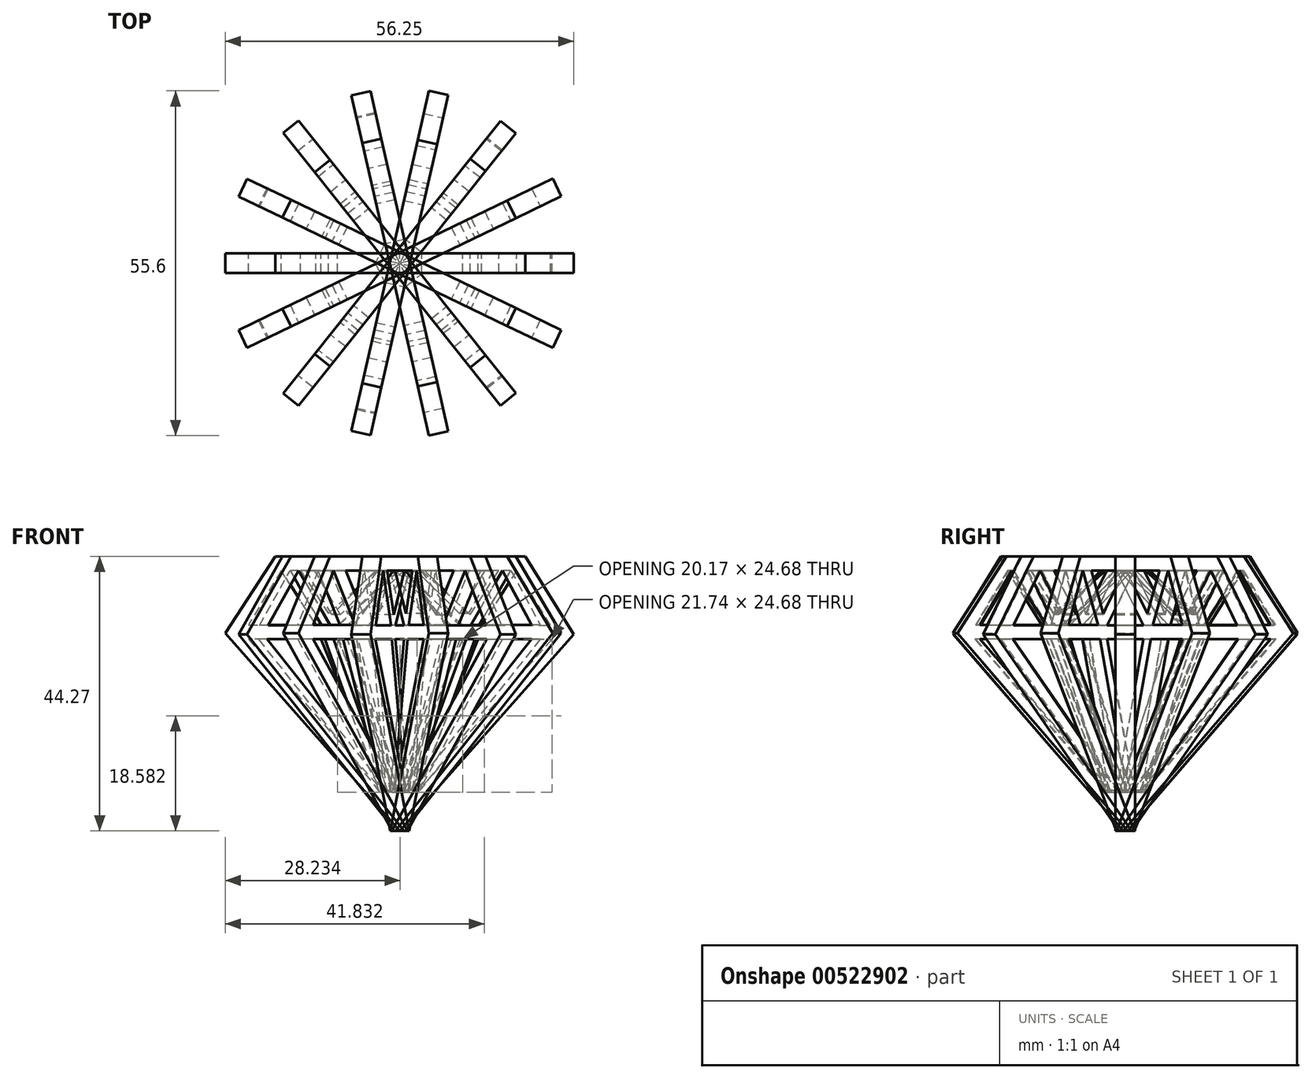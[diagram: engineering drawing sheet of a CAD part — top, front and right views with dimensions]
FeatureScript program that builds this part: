
annotation { "Feature Type Name" : "Feature", "Feature Type Description" : "" }
export const myFeature = defineFeature(function(context is Context, id is Id, definition is map)
    precondition{}
    {
        {
            var Q0;
            Q0=qCreatedBy(makeId("Front.planeOp"),FACE);
            var sketch = newSketch(context, id + "F0", { "sketchPlane" : qUnion([Q0])});
            skLineSegment(sketch, "E0", {"start": v(-12.69, 38.5) * mm, "end": v(-24.4, 38.5) * mm});
            skLineSegment(sketch, "E1", {"start": v(-24.4, 38.5) * mm, "end": v(-2.84, 14.13) * mm});
            skLineSegment(sketch, "E2", {"start": v(-2.84, 14.13) * mm, "end": v(-12.69, 38.5) * mm});
            skLineSegment(sketch, "E3", {"start": v(-10, 38.5) * mm, "end": v(0, 13.81) * mm});
            skLineSegment(sketch, "E4", {"start": v(0, 13.81) * mm, "end": v(10.16, 38.5) * mm});
            skLineSegment(sketch, "E5", {"start": v(10.16, 38.5) * mm, "end": v(-10, 38.5) * mm});
            skLineSegment(sketch, "E6", {"start": v(0, 49.57) * mm, "end": v(-10, 40.71) * mm});
            skLineSegment(sketch, "E7", {"start": v(-10, 40.71) * mm, "end": v(10.16, 40.71) * mm});
            skLineSegment(sketch, "E8", {"start": v(10.16, 40.71) * mm, "end": v(0, 49.57) * mm});
            skLineSegment(sketch, "E9", {"start": v(3.55, 49.57) * mm, "end": v(11.38, 42.44) * mm});
            skLineSegment(sketch, "E10", {"start": v(11.38, 42.44) * mm, "end": v(15.99, 49.57) * mm});
            skLineSegment(sketch, "E11", {"start": v(15.99, 49.57) * mm, "end": v(3.55, 49.57) * mm});
            skLineSegment(sketch, "E12", {"start": v(18.86, 49.57) * mm, "end": v(13.2, 40.71) * mm});
            skLineSegment(sketch, "E13", {"start": v(13.2, 40.71) * mm, "end": v(24.34, 40.71) * mm});
            skLineSegment(sketch, "E14", {"start": v(24.34, 40.71) * mm, "end": v(18.86, 49.57) * mm});
            skLineSegment(sketch, "E15", {"start": v(12.6, 38.5) * mm, "end": v(24.54, 38.5) * mm});
            skLineSegment(sketch, "E16", {"start": v(24.54, 38.5) * mm, "end": v(2.8, 13.81) * mm});
            skLineSegment(sketch, "E17", {"start": v(2.8, 13.81) * mm, "end": v(12.6, 38.5) * mm});
            skLineSegment(sketch, "E18", {"start": v(-11.5, 42.63) * mm, "end": v(-3.66, 49.57) * mm});
            skLineSegment(sketch, "E19", {"start": v(-3.66, 49.57) * mm, "end": v(-15.98, 49.57) * mm});
            skLineSegment(sketch, "E20", {"start": v(-15.98, 49.57) * mm, "end": v(-11.5, 42.63) * mm});
            skLineSegment(sketch, "E21", {"start": v(-19.13, 49.57) * mm, "end": v(-24.4, 40.79) * mm});
            skLineSegment(sketch, "E22", {"start": v(-24.4, 40.79) * mm, "end": v(-13.5, 40.79) * mm});
            skLineSegment(sketch, "E23", {"start": v(-13.5, 40.79) * mm, "end": v(-19.13, 49.57) * mm});
            skLineSegment(sketch, "E24", {"start": v(-20.04, 51.84) * mm, "end": v(-28.16, 39.44) * mm});
            skLineSegment(sketch, "E25", {"start": v(-28.16, 39.44) * mm, "end": v(0, 7.57) * mm});
            skLineSegment(sketch, "E26", {"start": v(0, 7.57) * mm, "end": v(28.1, 39.24) * mm});
            skLineSegment(sketch, "E27", {"start": v(28.1, 39.24) * mm, "end": v(20.25, 51.84) * mm});
            skLineSegment(sketch, "E28", {"start": v(20.25, 51.84) * mm, "end": v(-20.04, 51.84) * mm});
            skSolve(sketch);
        }
        {
            var Q0;
            Q0 = qSketchRegion(id + "F0", true);
            extrude(context, id + "F1", {"entities" : qUnion([Q0]), "endBound" : BoundingType.SYMMETRIC, "depth" : 3.17 * mm, "offsetDistance" : 25.4 * mm});
        }
        {
            var Q0;
            Q0=qCreatedBy(makeId("Front.planeOp"),FACE);
            var sketch = newSketch(context, id + "F2", { "sketchPlane" : qUnion([Q0])});
            skLineSegment(sketch, "E29", {"start": v(0, 0) * mm, "end": v(0, -23.74) * mm});
            skSolve(sketch);
        }
        {
            var Q0;
            Q0=makeQuery(id+"F1.opExtrude","SWEPT_BODY",BODY,{"disambiguationData":[OSD([sQuery(id+"F0.wireOp",EDGE,"E0"),sQuery(id+"F0.wireOp",EDGE,"E1"),sQuery(id+"F0.wireOp",EDGE,"E2"),sQuery(id+"F0.wireOp",EDGE,"E3"),sQuery(id+"F0.wireOp",EDGE,"E4"),sQuery(id+"F0.wireOp",EDGE,"E5"),sQuery(id+"F0.wireOp",EDGE,"E6"),sQuery(id+"F0.wireOp",EDGE,"E7"),sQuery(id+"F0.wireOp",EDGE,"E8"),sQuery(id+"F0.wireOp",EDGE,"E9"),sQuery(id+"F0.wireOp",EDGE,"E10"),sQuery(id+"F0.wireOp",EDGE,"E11"),sQuery(id+"F0.wireOp",EDGE,"E12"),sQuery(id+"F0.wireOp",EDGE,"E13"),sQuery(id+"F0.wireOp",EDGE,"E14"),sQuery(id+"F0.wireOp",EDGE,"E15"),sQuery(id+"F0.wireOp",EDGE,"E16"),sQuery(id+"F0.wireOp",EDGE,"E17"),sQuery(id+"F0.wireOp",EDGE,"E18"),sQuery(id+"F0.wireOp",EDGE,"E19"),sQuery(id+"F0.wireOp",EDGE,"E20"),sQuery(id+"F0.wireOp",EDGE,"E21"),sQuery(id+"F0.wireOp",EDGE,"E22"),sQuery(id+"F0.wireOp",EDGE,"E23"),sQuery(id+"F0.wireOp",EDGE,"E24"),sQuery(id+"F0.wireOp",EDGE,"E25"),sQuery(id+"F0.wireOp",EDGE,"E26"),sQuery(id+"F0.wireOp",EDGE,"E27"),sQuery(id+"F0.wireOp",EDGE,"E28")])]});
            var Q1;
            Q1=sQuery(id+"F2.wireOp",EDGE,"E29");
            circularPattern(context, id + "F3", {"entities" : qUnion([Q0]), "axis" : qUnion([Q1]), "angle" : 360 * degree, "instanceCount" : 7, "equalSpace" : true});
        }
    });
